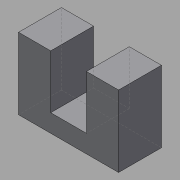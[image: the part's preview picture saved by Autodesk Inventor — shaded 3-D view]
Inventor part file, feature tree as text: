
AUTODESK INVENTOR PART (.ipt)
format: ipt  version: 2015 (Build 190159000, 159)  size: 77,824 bytes
history: native  units: in
note: dims shown in document units (in); Inventor stores cm internally (conversion verified against a paired STEP export)
features: other x3, sketch x2
ambient origin geometry x8: Origin, YZ Plane, XZ Plane, XY Plane, X Axis, Y Axis, Z Axis, Center Point
bodies: Solid1 (feature_tree)
feature tree (5):
  other  "opto.ipt"
  other  "Solid1::opto.ipt"
  other  "TaggingFeature1"
  sketch  "Sketch1"  dims[d0=0.3937in]
  sketch  "Sketch2"
